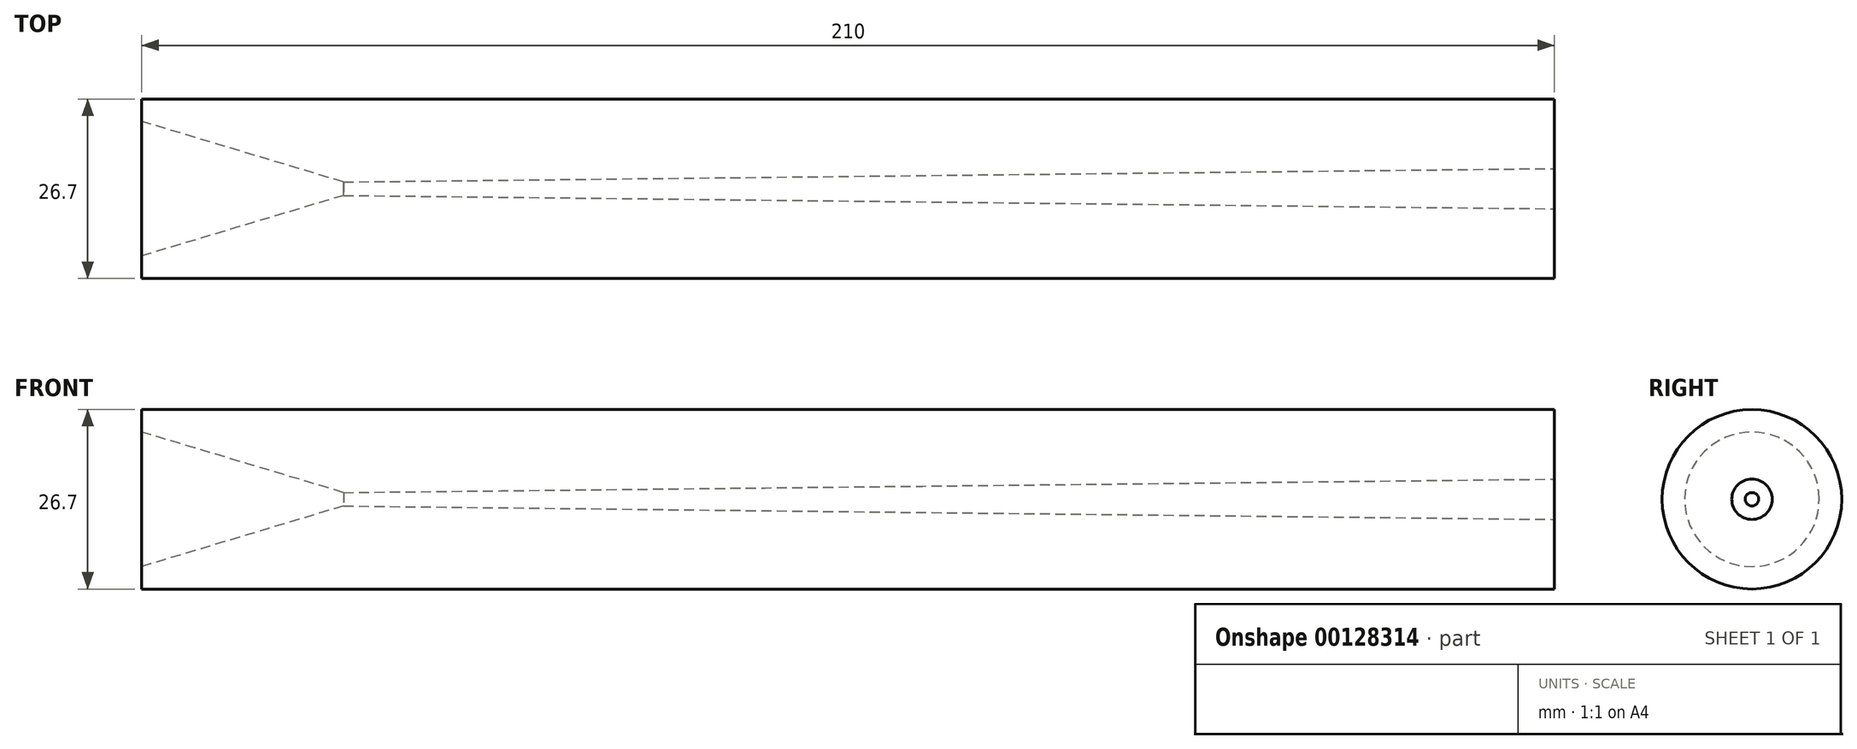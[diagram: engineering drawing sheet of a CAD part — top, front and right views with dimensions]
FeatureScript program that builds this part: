
annotation { "Feature Type Name" : "Feature", "Feature Type Description" : "" }
export const myFeature = defineFeature(function(context is Context, id is Id, definition is map)
    precondition{}
    {
        {
            var Q0;
            Q0=qCreatedBy(makeId("Front.planeOp"),FACE);
            var sketch = newSketch(context, id + "F0", { "sketchPlane" : qUnion([Q0])});
            skLineSegment(sketch, "E0.bottom", {"start": v(-30, 13.35) * mm, "end": v(180, 13.35) * mm});
            skLineSegment(sketch, "E0.top", {"start": v(-30, 0) * mm, "end": v(180, 0) * mm});
            skLineSegment(sketch, "E0.left", {"start": v(-30, 13.35) * mm, "end": v(-30, 0) * mm});
            skLineSegment(sketch, "E0.right", {"start": v(180, 13.35) * mm, "end": v(180, 0) * mm});
            skSolve(sketch);
        }
        {
            var Q0;
            Q0 = qSketchRegion(id + "F0", true);
            var Q1;
            Q1=sQuery(id+"F0.wireOp",EDGE,"E0.top");
            revolve(context, id + "F1", {"entities" : qUnion([Q0]), "axis" : qUnion([Q1]), "revolveType" : RevolveType.FULL});
        }
        {
            var Q0;
            Q0=qCreatedBy(makeId("Front.planeOp"),FACE);
            var sketch = newSketch(context, id + "F2", { "sketchPlane" : qUnion([Q0])});
            skLineSegment(sketch, "E1", {"start": v(-30, 10) * mm, "end": v(0, 1) * mm});
            skLineSegment(sketch, "E2", {"start": v(0, 1) * mm, "end": v(180, 3) * mm});
            skLineSegment(sketch, "E3", {"start": v(180, 0) * mm, "end": v(-30, 0) * mm});
            skLineSegment(sketch, "E4", {"start": v(-30, 0) * mm, "end": v(-30, 10) * mm});
            skLineSegment(sketch, "E5", {"start": v(180, 3) * mm, "end": v(180, 0) * mm});
            skSolve(sketch);
        }
        {
            var Q0;
            Q0 = qSketchRegion(id + "F2", true);
            var Q1;
            Q1=sQuery(id+"F2.wireOp",EDGE,"E3");
            revolve(context, id + "F3", {"operationType" : NewBodyOperationType.REMOVE, "entities" : qUnion([Q0]), "axis" : qUnion([Q1]), "revolveType" : RevolveType.FULL, "oppositeDirection" : true});
        }
    });
